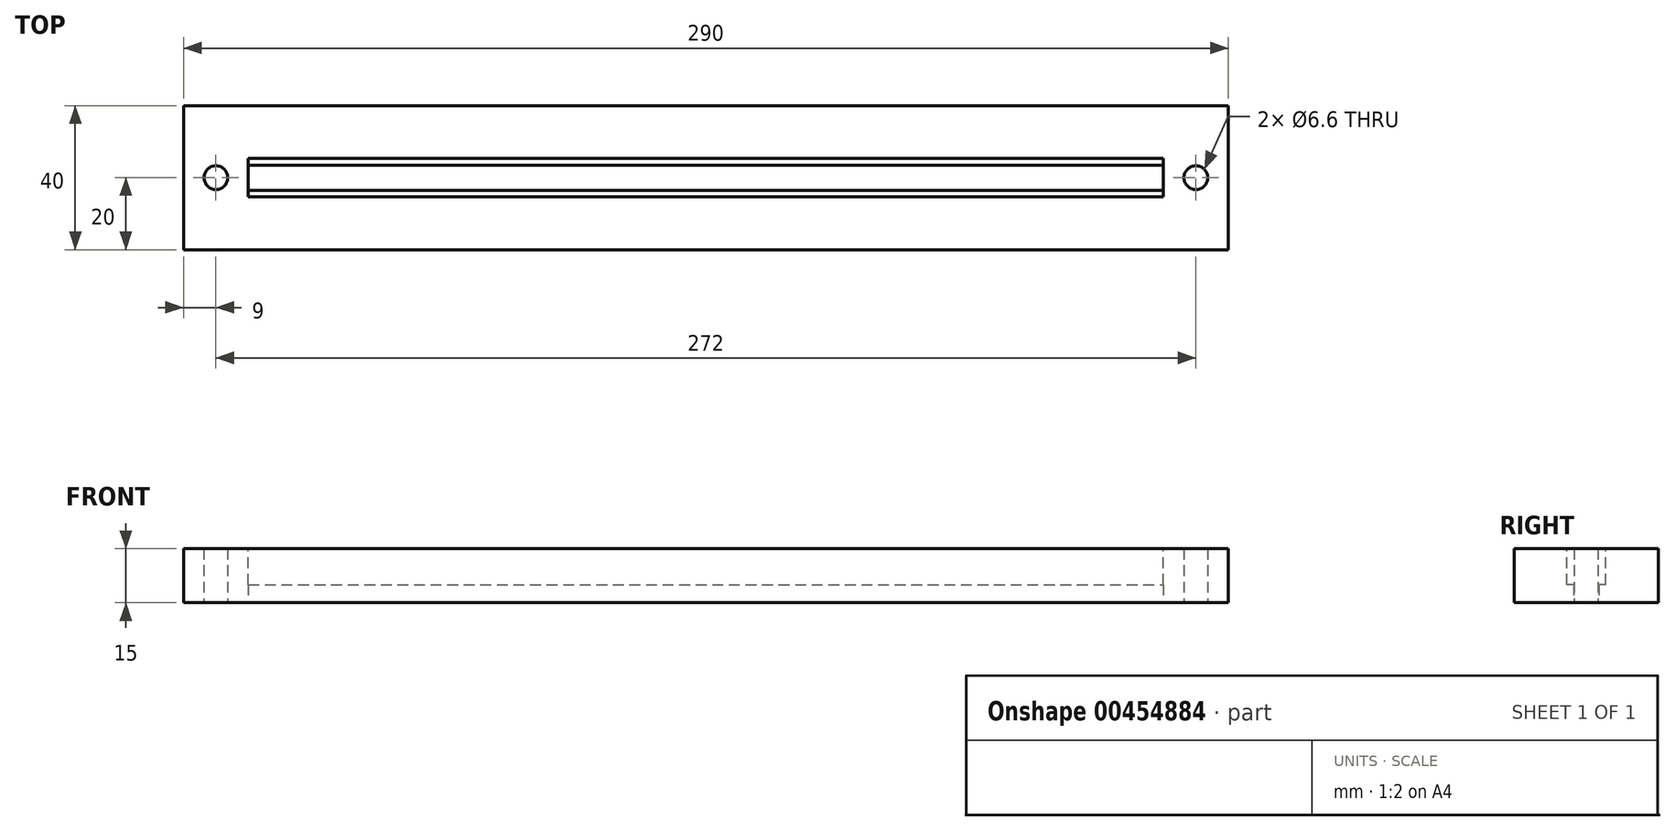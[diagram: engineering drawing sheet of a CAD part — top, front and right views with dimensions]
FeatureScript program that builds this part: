
annotation { "Feature Type Name" : "Feature", "Feature Type Description" : "" }
export const myFeature = defineFeature(function(context is Context, id is Id, definition is map)
    precondition{}
    {
        {
            var Q0;
            Q0=qCreatedBy(makeId("Top.planeOp"),FACE);
            var sketch = newSketch(context, id + "F0", { "sketchPlane" : qUnion([Q0])});
            skLineSegment(sketch, "E0.bottom", {"start": v(-145, 20) * mm, "end": v(145, 20) * mm});
            skLineSegment(sketch, "E0.top", {"start": v(-145, -20) * mm, "end": v(145, -20) * mm});
            skLineSegment(sketch, "E0.left", {"start": v(-145, 20) * mm, "end": v(-145, -20) * mm});
            skLineSegment(sketch, "E0.right", {"start": v(145, 20) * mm, "end": v(145, -20) * mm});
            skLineSegment(sketch, "E1.bottom", {"start": v(-127, 3.5) * mm, "end": v(127, 3.5) * mm});
            skLineSegment(sketch, "E1.top", {"start": v(-127, -3.5) * mm, "end": v(127, -3.5) * mm});
            skLineSegment(sketch, "E1.left", {"start": v(-127, 0) * mm, "end": v(-127, 0) * mm});
            skLineSegment(sketch, "E1.right", {"start": v(127, 0) * mm, "end": v(127, 0) * mm});
            skLineSegment(sketch, "E2", {"start": v(127, 3.5) * mm, "end": v(127, -3.5) * mm});
            skLineSegment(sketch, "E3", {"start": v(-127, -3.5) * mm, "end": v(-127, -3.5) * mm});
            skLineSegment(sketch, "E4", {"start": v(-127, -3.5) * mm, "end": v(-127, 3.5) * mm});
            skLineSegment(sketch, "E5", {"start": v(-127, 3.5) * mm, "end": v(-127, 3.5) * mm});
            skSolve(sketch);
        }
        {
            var Q0;
            Q0=makeQuery(id+"F0.imprint","IMPRINT",FACE,{"disambiguationData":[TD([[makeQuery(id+"F0.imprint","IMPRINT",EDGE,{"derivedFrom":sQuery(id+"F0.wireOp",EDGE,"E0.bottom")}),-1.0]])]});
            extrude(context, id + "F1", {"entities" : qUnion([Q0]), "depth" : 15 * mm});
        }
        {
            var Q0;
            Q0=makeQuery(id+"F1.opExtrude","CAP_FACE",FACE,{"disambiguationData":[OSD([sQuery(id+"F0.wireOp",EDGE,"E0.bottom"),sQuery(id+"F0.wireOp",EDGE,"E0.top"),sQuery(id+"F0.wireOp",EDGE,"E0.left"),sQuery(id+"F0.wireOp",EDGE,"E0.right"),sQuery(id+"F0.wireOp",EDGE,"E1.bottom"),sQuery(id+"F0.wireOp",EDGE,"E1.top"),sQuery(id+"F0.wireOp",EDGE,"229ee3cc-ec6f-48da-86d1-11e76dc9f06e.filletArc"),sQuery(id+"F0.wireOp",EDGE,"f5671cc3-9e84-4852-b088-b8cc9d101e9e.filletArc"),sQuery(id+"F0.wireOp",EDGE,"d9a9eb8b-dc08-4419-bcfd-51e643ab69b2.filletArc"),sQuery(id+"F0.wireOp",EDGE,"c6b41233-c76c-471e-9b99-d7ce40cc7d49.filletArc")])],"isStart":false});
            var sketch = newSketch(context, id + "F2", { "sketchPlane" : qUnion([Q0])});
            skLineSegment(sketch, "E6.bottom", {"start": v(-127, 5.35) * mm, "end": v(127, 5.35) * mm});
            skLineSegment(sketch, "E6.top", {"start": v(-127, -5.35) * mm, "end": v(127, -5.35) * mm});
            skLineSegment(sketch, "E6.left", {"start": v(-127, 5.35) * mm, "end": v(-127, -5.35) * mm});
            skLineSegment(sketch, "E6.right", {"start": v(127, 5.35) * mm, "end": v(127, -5.35) * mm});
            skSolve(sketch);
        }
        {
            var Q0;
            {var subQ1=sQuery(id+"F2.wireOp",EDGE,"E6.bottom");Q0=makeQuery(id+"F2.imprint","IMPRINT",FACE,{"disambiguationData":[TD([[makeQuery(id+"F2.imprint","IMPRINT",EDGE,{"derivedFrom":subQ1}),-1.0]])]});}
            var Q1;
            {var subQ1=sQuery(id+"F2.wireOp",EDGE,"E6.top");Q1=makeQuery(id+"F2.imprint","IMPRINT",FACE,{"disambiguationData":[TD([[makeQuery(id+"F2.imprint","IMPRINT",EDGE,{"derivedFrom":subQ1}),1.0]])]});}
            extrude(context, id + "F3", {"entities" : qUnion([Q0, Q1]), "operationType" : NewBodyOperationType.REMOVE, "oppositeDirection" : true, "depth" : 10 * mm});
        }
        {
            var Q0;
            Q0=makeQuery(id+"F1.opExtrude","CAP_FACE",FACE,{"disambiguationData":[OSD([sQuery(id+"F0.wireOp",EDGE,"E0.bottom"),sQuery(id+"F0.wireOp",EDGE,"E0.top"),sQuery(id+"F0.wireOp",EDGE,"E0.left"),sQuery(id+"F0.wireOp",EDGE,"E0.right"),sQuery(id+"F0.wireOp",EDGE,"E1.bottom"),sQuery(id+"F0.wireOp",EDGE,"E1.top"),sQuery(id+"F0.wireOp",EDGE,"E2"),sQuery(id+"F0.wireOp",EDGE,"E4")])],"isStart":true});
            var sketch = newSketch(context, id + "F4", { "sketchPlane" : qUnion([Q0])});
            skCircle(sketch, "E7", {"center": v(136, 0) * mm, "radius": 3.3 * mm});
            skPoint(sketch, "E7.centerSnap0", {"position": v(127, 0) * mm});
            skCircle(sketch, "E8", {"center": v(-136, 0) * mm, "radius": 3.3 * mm});
            skPoint(sketch, "E8.centerSnap0", {"position": v(-127, 0) * mm});
            skSolve(sketch);
        }
        {
            var Q0;
            Q0=makeQuery(id+"F4.imprint","IMPRINT",FACE,{"disambiguationData":[TD([[makeQuery(id+"F4.imprint","IMPRINT",EDGE,{"derivedFrom":sQuery(id+"F4.wireOp",EDGE,"E8")}),1.0]])]});
            var Q1;
            Q1=makeQuery(id+"F4.imprint","IMPRINT",FACE,{"disambiguationData":[TD([[makeQuery(id+"F4.imprint","IMPRINT",EDGE,{"derivedFrom":sQuery(id+"F4.wireOp",EDGE,"E7")}),1.0]])]});
            extrude(context, id + "F5", {"entities" : qUnion([Q0, Q1]), "operationType" : NewBodyOperationType.REMOVE, "endBound" : BoundingType.UP_TO_NEXT, "oppositeDirection" : true, "depth" : 25 * mm});
        }
    });
